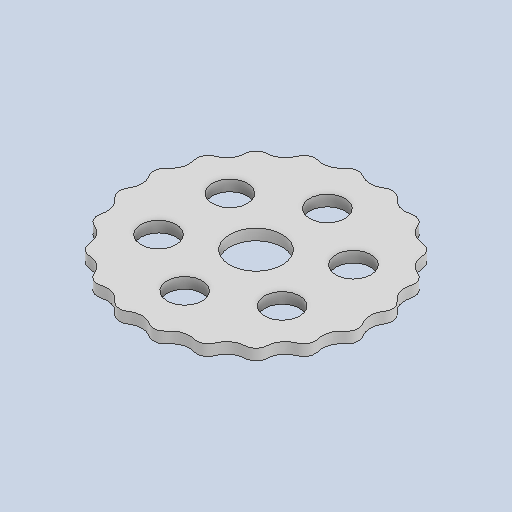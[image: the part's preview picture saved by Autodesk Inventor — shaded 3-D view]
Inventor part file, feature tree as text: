
AUTODESK INVENTOR PART (.ipt)
format: ipt  version: 2023 (Build 270158000, 158)  size: 354,304 bytes
history: native  units: in
note: dims shown in document units (in); Inventor stores cm internally (conversion verified against a paired STEP export)
features: extrude x2, sketch x2, other x1
ambient origin geometry x8: Origin, YZ Plane, XZ Plane, XY Plane, X Axis, Y Axis, Z Axis, Center Point
bodies: Body1 (feature_tree)
feature tree (5):
  extrude  "Extrusion2"  Depth=0.1969in TaperAngle=0.0deg
  extrude  "Extrusion3"  Depth=0.6299in
  sketch  "Sketch2"  dims[d6=0.0in d7=141.3386in d8=0.1969in d9=0.0in]
  other  "2D Equation Curve3"
  sketch  "Sketch3"  dims[d10=0.9449in d11=0.6299in d12=2.5591in d13=2.3622in d15=360.0deg d17=0.0in d18=0.0in d20=0.5709in d21=0.8661in]
